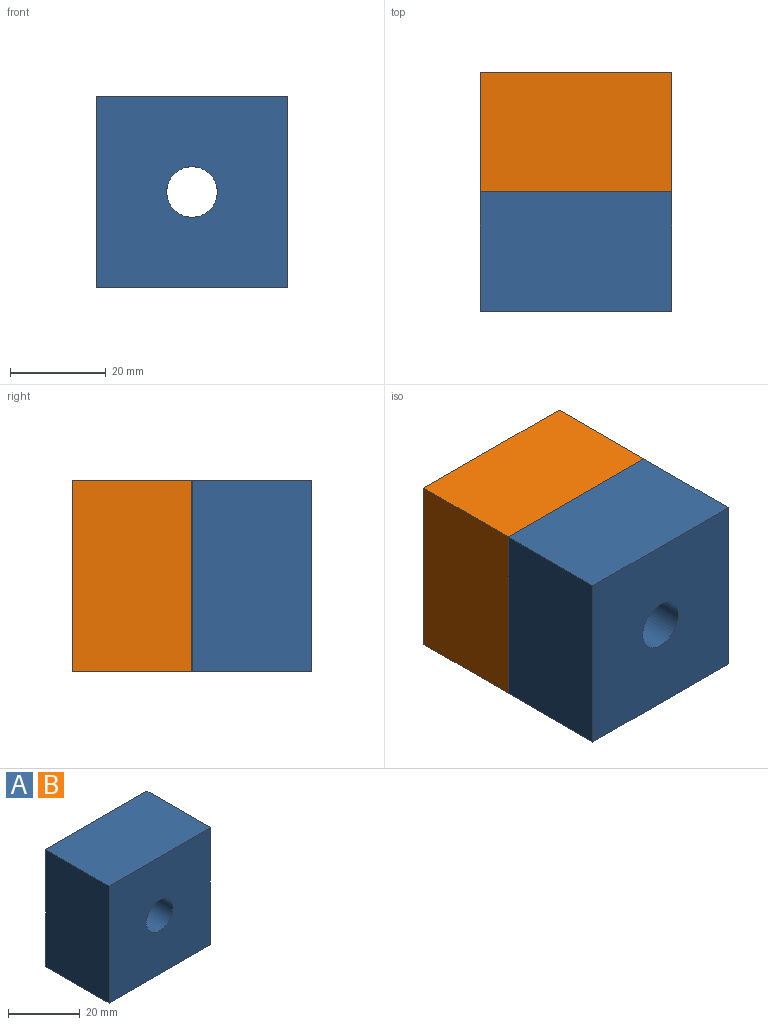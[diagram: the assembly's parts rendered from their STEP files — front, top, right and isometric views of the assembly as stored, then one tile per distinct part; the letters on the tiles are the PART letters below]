
ASSEMBLY  parts=2 mates=1
PART A: 7 faces, bbox 40x25x40 mm
  f0: plane 40x25mm, normal (1,0,0), area 1000mm2, adj f1,f3,f5,f6
  f1: plane 40x25mm, normal (0,0,1), area 1000mm2, adj f0,f2,f5,f6
  f2: plane 40x25mm, normal (-1,0,0), area 1000mm2, adj f1,f3,f5,f6
  f3: plane 40x25mm, normal (0,0,-1), area 1000mm2, adj f0,f2,f5,f6
  f4: cylinder r=5.29mm len=25mm, axis (0,1,0), area 830.7mm2, adj f5,f6
  f5: plane 40x40mm, normal (0,-1,0), area 1512.1mm2, adj f0,f1,f2,f3,f4
  f6: plane 40x40mm, normal (0,1,0), area 1512.1mm2, adj f0,f1,f2,f3,f4
PART B: same geometry as A
PLACE A rot(axis=(1,0,0),180deg) t=(1.49,-36.41,0.35)mm
PLACE B t=(1.49,13.59,0.35)mm
MATE revolute A.f4 <-> B.f4  axis (0,1,0) through (1.49,-11.41,0.35)mm
